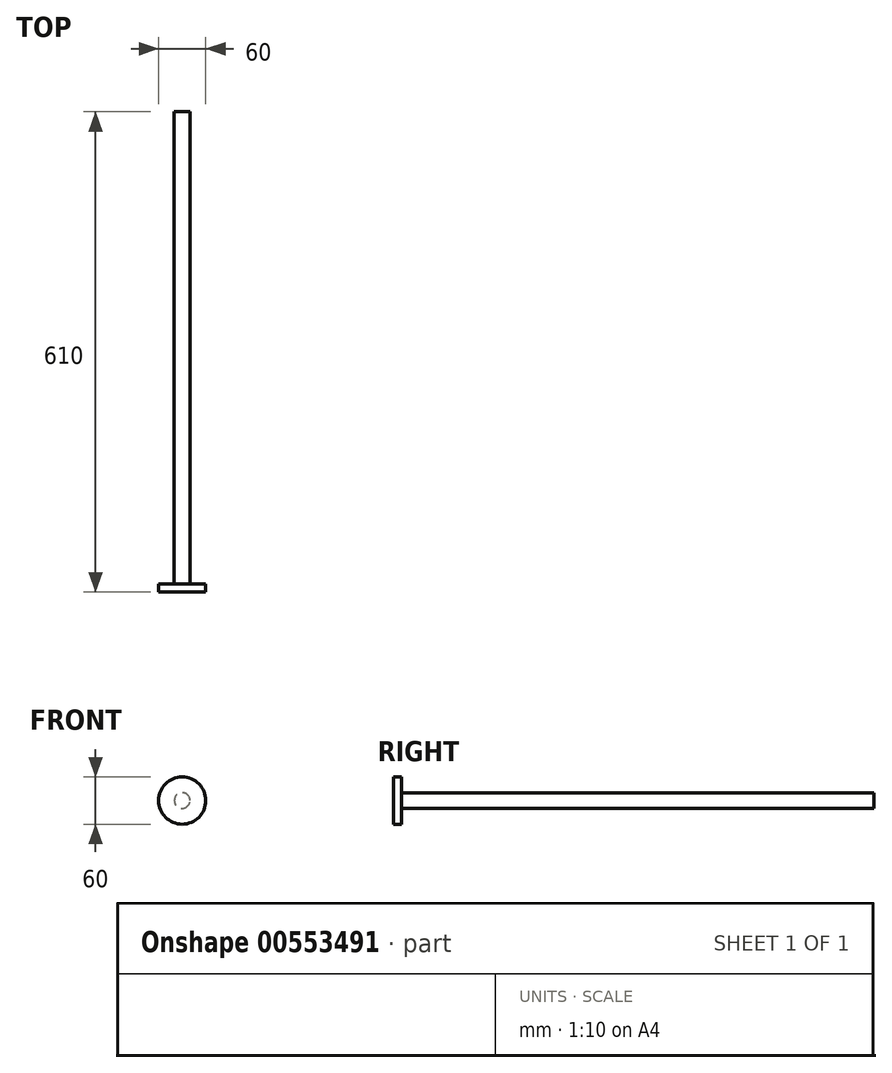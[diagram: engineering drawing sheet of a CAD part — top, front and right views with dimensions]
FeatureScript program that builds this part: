
annotation { "Feature Type Name" : "Feature", "Feature Type Description" : "" }
export const myFeature = defineFeature(function(context is Context, id is Id, definition is map)
    precondition{}
    {
        {
            var Q0;
            Q0=qCreatedBy(makeId("Front.planeOp"),FACE);
            var sketch = newSketch(context, id + "F0", { "sketchPlane" : qUnion([Q0])});
            skCircle(sketch, "E0", {"center": v(0, 0) * mm, "radius": 10 * mm});
            skSolve(sketch);
        }
        {
            var Q0;
            Q0=qSketchRegion(id+"F0",true);
            extrude(context, id + "F1", {"entities" : qUnion([Q0]), "depth" : 600 * mm});
        }
        {
            var Q0;
            Q0=makeQuery(id+"F1.opExtrude","CAP_FACE",FACE,{"disambiguationData":[OSD([sQuery(id+"F0.wireOp",EDGE,"E0")])],"isStart":false});
            var sketch = newSketch(context, id + "F2", { "sketchPlane" : qUnion([Q0])});
            skCircle(sketch, "E1", {"center": v(0, 0) * mm, "radius": 30 * mm});
            skSolve(sketch);
        }
        {
            var Q0;
            Q0=qSketchRegion(id+"F2",true);
            extrude(context, id + "F3", {"entities" : qUnion([Q0]), "depth" : 10 * mm, "offsetDistance" : 25 * mm});
        }
    });
